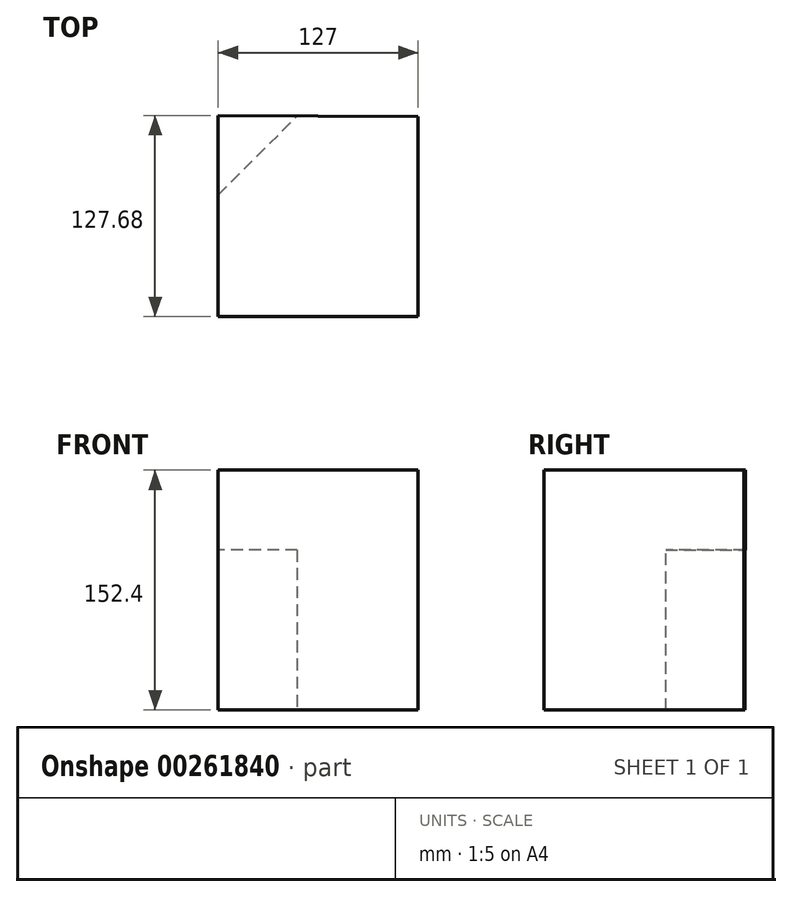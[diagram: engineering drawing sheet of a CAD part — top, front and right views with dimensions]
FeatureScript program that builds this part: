
annotation { "Feature Type Name" : "Feature", "Feature Type Description" : "" }
export const myFeature = defineFeature(function(context is Context, id is Id, definition is map)
    precondition{}
    {
        {
            var Q0;
            Q0=qCreatedBy(makeId("Top.planeOp"),FACE);
            var sketch = newSketch(context, id + "F0", { "sketchPlane" : qUnion([Q0])});
            skLineSegment(sketch, "E0", {"start": v(-63.82, 63.87) * mm, "end": v(-63.82, -63.81) * mm});
            skLineSegment(sketch, "E1", {"start": v(-63.82, -63.81) * mm, "end": v(63.18, -63.81) * mm});
            skLineSegment(sketch, "E2", {"start": v(63.18, -63.81) * mm, "end": v(63.18, 63.19) * mm});
            skLineSegment(sketch, "E3", {"start": v(63.18, 63.19) * mm, "end": v(-63.82, 63.87) * mm});
            skSolve(sketch);
        }
        {
            var Q0;
            Q0=makeQuery(id+"F0.imprint","IMPRINT",FACE,{"disambiguationData":[TD([[makeQuery(id+"F0.imprint","IMPRINT",EDGE,{"derivedFrom":sQuery(id+"F0.wireOp",EDGE,"E0")}),1.0]])]});
            var sketch = newSketch(context, id + "F1", { "sketchPlane" : qUnion([Q0])});
            skLineSegment(sketch, "E4", {"start": v(-64.08, 63.98) * mm, "end": v(-64.08, 13.18) * mm});
            skLineSegment(sketch, "E5", {"start": v(-64.08, 63.98) * mm, "end": v(-13.28, 63.98) * mm});
            skLineSegment(sketch, "E6", {"start": v(-64.08, 13.18) * mm, "end": v(-13.28, 63.98) * mm});
            skSolve(sketch);
        }
        {
            var Q0;
            Q0 = qSketchRegion(id + "F0", true);
            extrude(context, id + "F2", {"entities" : qUnion([Q0]), "depth" : 152.4 * mm});
        }
        {
            var Q0;
            Q0 = qSketchRegion(id + "F1", true);
            extrude(context, id + "F3", {"entities" : qUnion([Q0]), "operationType" : NewBodyOperationType.REMOVE, "depth" : 101.6 * mm});
        }
    });
